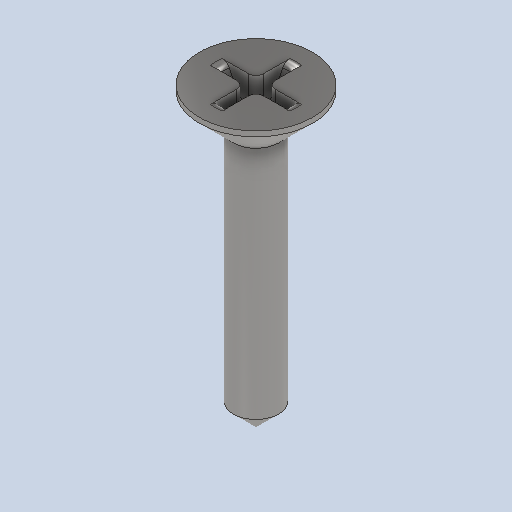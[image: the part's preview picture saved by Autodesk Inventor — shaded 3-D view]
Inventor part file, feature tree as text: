
AUTODESK INVENTOR PART (.ipt)
format: ipt  version: 2022 (Build 260153000, 153)  size: 187,392 bytes
history: native  units: mm
features: sketch x2, revolve x1, extrude x1, fillet x1
ambient origin geometry x8: Origin, YZ Plane, XZ Plane, XY Plane, X Axis, Y Axis, Z Axis, Center Point
bodies: Solid1 (feature_tree)
feature tree (5):
  revolve  "Revolution1"  [1 undecoded]
  extrude  "Extrusion1"  TaperAngle=60.0deg  [1 undecoded]
  fillet  "Fillet1"  [1 undecoded]
  sketch  "Sketch1"  dims[d0=3.625mm d1=2.25mm]
  sketch  "Sketch2"  dims[d2=19.0mm d3=60.0deg d4=45.0deg d5=2.5mm d6=2.5mm d7=4.363323mm d8=90.0deg d9=0.375mm d10=0.75mm d11=1.875mm d12=1.875mm d13=0.75mm d14=1.875mm d15=1.875mm d16=0.5mm d17=10.0mm d18=0.0mm d19=0.5mm]
note: 3 required parameter values undecoded (feature->parameter linkage not recoverable at this tier; creation-order binding heuristic only, values carry confidence <= 0.55)